# Revit family: MUY-TP35VF
name_source: partatom
category: Mechanical Equipment
revit_build: Autodesk Revit 2016 (Build: 20150714_1515(x64)
units: mm (PartAtom-declared; Revit-internal decimal feet)

## family parameters
Always vertical = Yes
Cut with Voids When Loaded = No
OmniClass Number = 23.75.00.00
OmniClass Title = Climate Control (HVAC)
Part Type = Normal
Room Calculation Point = No
Round Connector Dimension = Use Radius
Shared = No
Work Plane-Based = No

## types (1)
- MUY-TP35VF
    Breaker Capacity (A) = 10
    Compressor Cooling Current (A) = 3.6
    Compressor Model = SVB130FBBMT
    Compressor Output (W) = 900
    Compressor Refrigeration oil (Model) = 0.35 (FW68S)
    Cooling Air Flow_High (m3/h) = 1758
    Cooling Air Flow_Low (m3/h) = 984
    Cooling Capacity Rated frequency (Min.-Max.) (kW) = 3.5 (1.5-4.0)
    Cooling Coefficient of performance (COP) (Set) = 4.61
    Cooling Dehumidification (L/h) = 0.1
    Cooling Fan Speed_High (rpm) = 810
    Cooling Fan Speed_Low (rpm) = 490
    Cooling Power factor (Set) (%) = 91
    Cooling Power input (Set) (W) = 760
    Cooling Running current (Set) (A) = 3.6
    Cooling Sound Level (dB(A)) = 45
    Depth (mm) = 285 mm  [stored 0.935039 ft]
    Fan Motor Cooling Current (A) = 0.21
    Fan motor Model = RC0J50-NC
    Fan speed regulator = 3
    Gas pipe_radius (mm) = 5 mm  [stored 0.0164042 ft]
    Height (mm) = 550 mm
    Hertz = 50 Hz
    Liquid pipe_radius (mm) = 3 mm  [stored 0.00984252 ft]
    Manufacturer = Mitsubishi Electric Corporation
    Model = MUY-TP35VF
    Phase = 1
    Refrigerant filling capacity (kg) = 0.85
    Refrigerant type = R32
    Space View = Yes
    Starting current (Set) (A) = 3.6
    Subcategory = HVAC
    URL = http://www.mitsubishielectric.com
    Unit Weight (kg) = 34.00 kg
    Voltage = 230 V
    Width (mm) = 800 mm  [stored 2.62467 ft]

note: [stored X ft] marks values corroborated as IEEE doubles in the binary element streams (Revit-internal decimal feet)

## geometry (parser evidence)
native form markers: Blend x40, Sweep x2
no freeform markers — native parametric forms only
